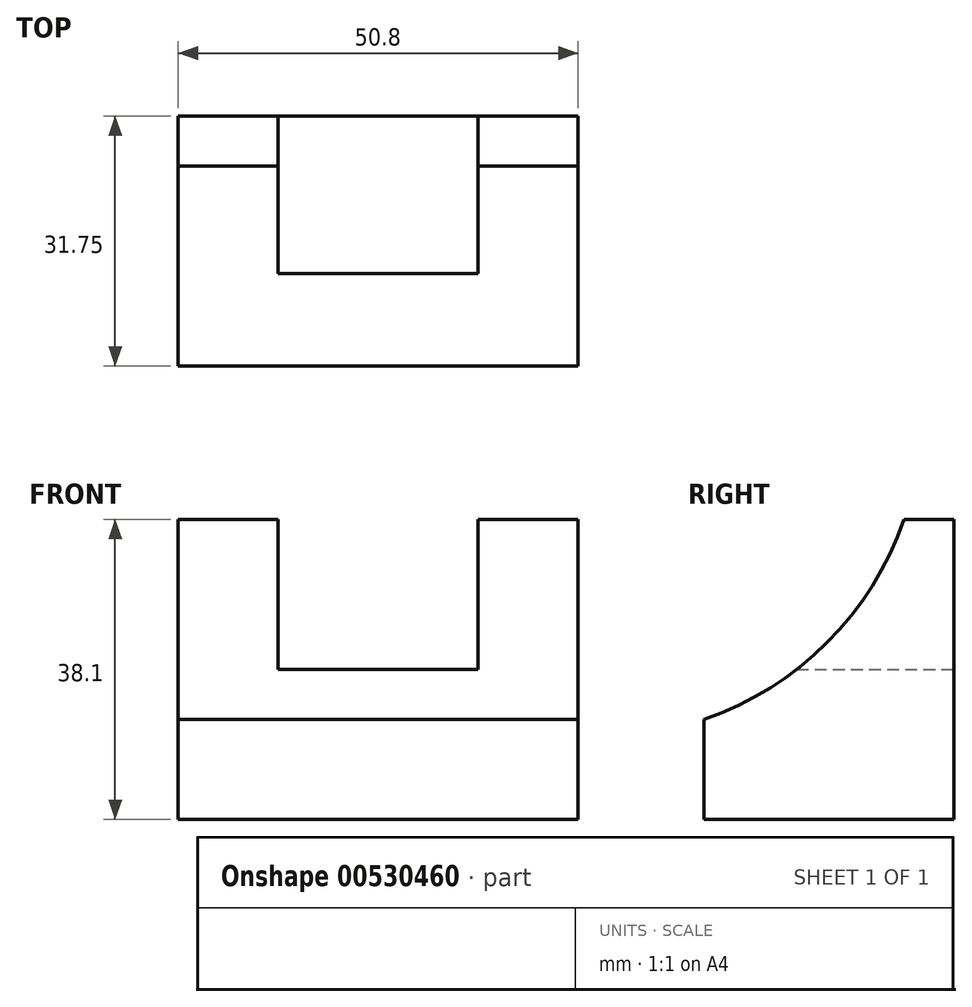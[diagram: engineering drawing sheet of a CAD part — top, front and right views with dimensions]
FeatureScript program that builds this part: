
annotation { "Feature Type Name" : "Feature", "Feature Type Description" : "" }
export const myFeature = defineFeature(function(context is Context, id is Id, definition is map)
    precondition{}
    {
        {
            var Q0;
            Q0=qCreatedBy(makeId("Front.planeOp"),FACE);
            var sketch = newSketch(context, id + "F0", { "sketchPlane" : qUnion([Q0])});
            skLineSegment(sketch, "E0", {"start": v(-59.79, 45.14) * mm, "end": v(-59.79, 7.04) * mm});
            skLineSegment(sketch, "E1", {"start": v(-59.79, 7.04) * mm, "end": v(-8.99, 7.04) * mm});
            skLineSegment(sketch, "E2", {"start": v(-8.99, 7.04) * mm, "end": v(-8.99, 45.14) * mm});
            skLineSegment(sketch, "E3", {"start": v(-8.99, 45.14) * mm, "end": v(-59.79, 45.14) * mm});
            skSolve(sketch);
        }
        {
            var Q0;
            Q0=makeQuery(id+"F0.imprint","IMPRINT",FACE,{"disambiguationData":[TD([[makeQuery(id+"F0.imprint","IMPRINT",EDGE,{"derivedFrom":sQuery(id+"F0.wireOp",EDGE,"E0")}),1.0]])]});
            extrude(context, id + "F1", {"entities" : qUnion([Q0]), "depth" : 31.75 * mm, "offsetDistance" : 25.4 * mm});
        }
        {
            var Q0;
            Q0=makeQuery(id+"F1.opExtrude","SWEPT_FACE",FACE,{"disambiguationData":[OSD([sQuery(id+"F0.wireOp",EDGE,"E2")])]});
            var sketch = newSketch(context, id + "F2", { "sketchPlane" : qUnion([Q0])});
            skArc(sketch, "E4", {"start": v(-31.75, 19.74) * mm, "mid": v(-16.11, 29.5) * mm, "end": v(-6.35, 45.14) * mm});
            skSolve(sketch);
        }
        {
            var Q0;
            Q0 = qSketchRegion(id + "F2", true);
            var Q1;
            {var subQ0=sQuery(id+"F2.wireOp",EDGE,"E4");Q1=makeQuery(id+"F2.imprint","IMPRINT",FACE,{"disambiguationData":[TD([[makeQuery(id+"F2.imprint","IMPRINT",EDGE,{"derivedFrom":subQ0}),1.0]])]});}
            extrude(context, id + "F3", {"entities" : qUnion([Q0, Q1]), "operationType" : NewBodyOperationType.REMOVE, "endBound" : BoundingType.THROUGH_ALL, "oppositeDirection" : true, "depth" : 25.4 * mm, "offsetDistance" : 25.4 * mm});
        }
        {
            var Q0;
            Q0=makeQuery(id+"F1.opExtrude","CAP_FACE",FACE,{"disambiguationData":[OSD([sQuery(id+"F0.wireOp",EDGE,"E0"),sQuery(id+"F0.wireOp",EDGE,"E1"),sQuery(id+"F0.wireOp",EDGE,"E2"),sQuery(id+"F0.wireOp",EDGE,"E3")])],"isStart":true});
            var sketch = newSketch(context, id + "F4", { "sketchPlane" : qUnion([Q0])});
            skLineSegment(sketch, "E5", {"start": v(21.69, 45.14) * mm, "end": v(21.69, 26.1) * mm});
            skLineSegment(sketch, "E6", {"start": v(21.69, 26.1) * mm, "end": v(47.09, 26.1) * mm});
            skLineSegment(sketch, "E7", {"start": v(47.09, 26.1) * mm, "end": v(47.09, 45.14) * mm});
            skSolve(sketch);
        }
        {
            var Q0;
            {var subQ0=sQuery(id+"F4.wireOp",EDGE,"E5");Q0=makeQuery(id+"F4.imprint","IMPRINT",FACE,{"disambiguationData":[TD([[makeQuery(id+"F4.imprint","IMPRINT",EDGE,{"derivedFrom":subQ0}),1.0]])]});}
            extrude(context, id + "F5", {"entities" : qUnion([Q0]), "operationType" : NewBodyOperationType.REMOVE, "endBound" : BoundingType.THROUGH_ALL, "oppositeDirection" : true, "depth" : 25.4 * mm, "offsetDistance" : 25.4 * mm});
        }
    });
